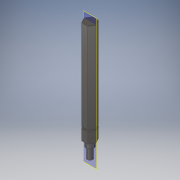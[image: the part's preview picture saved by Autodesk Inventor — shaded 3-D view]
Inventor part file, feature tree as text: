
AUTODESK INVENTOR PART (.ipt)
format: ipt  version: 2017.1 (Build 211199000, 199)  size: 129,024 bytes
history: native  units: in
note: dims shown in document units (in); Inventor stores cm internally (conversion verified against a paired STEP export)
features: plane x1, chamfer x1
ambient origin geometry x8: Origin, YZ Plane, XZ Plane, XY Plane, X Axis, Y Axis, Z Axis, Center Point
bodies: Solid1 (feature_tree)
feature tree (2):
  plane  "Work Plane1"
  chamfer  "Chamfer1"  [1 undecoded]
note: 1 required parameter value undecoded (feature->parameter linkage not recoverable at this tier; creation-order binding heuristic only, values carry confidence <= 0.55)
